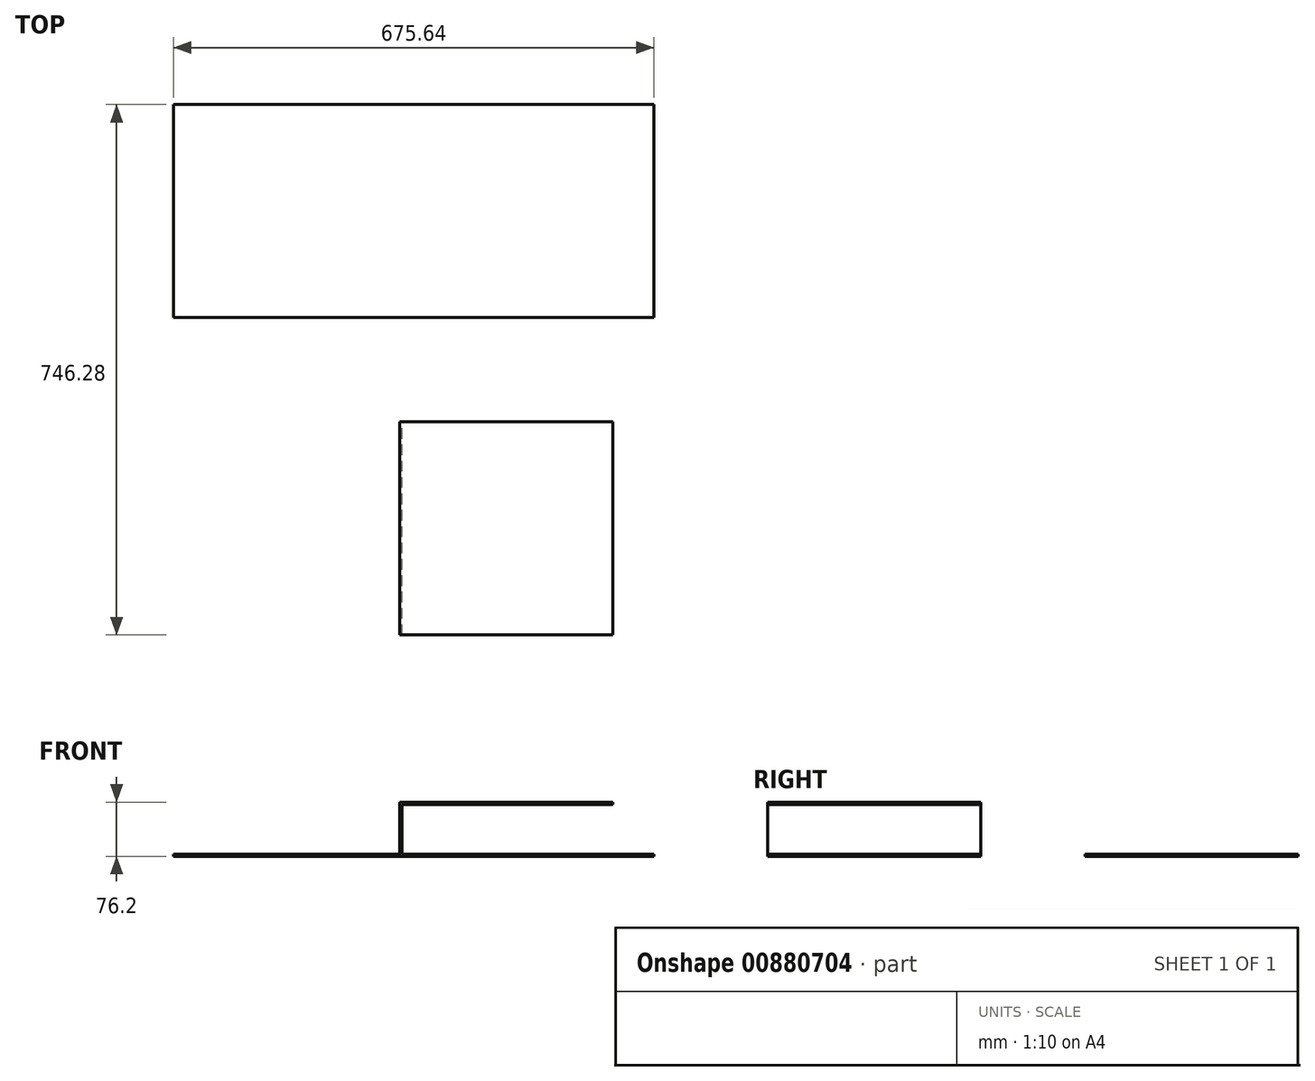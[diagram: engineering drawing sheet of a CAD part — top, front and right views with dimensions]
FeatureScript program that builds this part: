
annotation { "Feature Type Name" : "Feature", "Feature Type Description" : "" }
export const myFeature = defineFeature(function(context is Context, id is Id, definition is map)
    precondition{}
    {
        {
            var Q0;
            Q0=qCreatedBy(makeId("Front.planeOp"),FACE);
            var sketch = newSketch(context, id + "F0", { "sketchPlane" : qUnion([Q0])});
            skLineSegment(sketch, "E0", {"start": v(0, 0) * mm, "end": v(0, 76.2) * mm});
            skLineSegment(sketch, "E1", {"start": v(0, 76.2) * mm, "end": v(299.72, 76.2) * mm});
            skLineSegment(sketch, "E2", {"start": v(299.72, 76.2) * mm, "end": v(299.72, 73.03) * mm});
            skLineSegment(sketch, "E3", {"start": v(299.72, 73.03) * mm, "end": v(3.17, 73.02) * mm});
            skLineSegment(sketch, "E4", {"start": v(3.17, 73.02) * mm, "end": v(3.17, 3.17) * mm});
            skLineSegment(sketch, "E5", {"start": v(3.17, 3.17) * mm, "end": v(299.72, 3.18) * mm});
            skLineSegment(sketch, "E6", {"start": v(299.72, 3.18) * mm, "end": v(299.72, 0) * mm});
            skLineSegment(sketch, "E7", {"start": v(299.72, 0) * mm, "end": v(0, 0) * mm});
            skSolve(sketch);
        }
        {
            var Q0;
            Q0=makeQuery(id+"F0.imprint","IMPRINT",FACE,{"disambiguationData":[TD([[makeQuery(id+"F0.imprint","IMPRINT",EDGE,{"derivedFrom":sQuery(id+"F0.wireOp",EDGE,"E0")}),-1.0]])]});
            extrude(context, id + "F1", {"entities" : qUnion([Q0]), "depth" : 299.72 * mm, "offsetDistance" : 25.4 * mm});
        }
        {
            var Q0;
            Q0=qCreatedBy(makeId("Top.planeOp"),FACE);
            var sketch = newSketch(context, id + "F2", { "sketchPlane" : qUnion([Q0])});
            skLineSegment(sketch, "E8", {"start": v(-317.91, 146.84) * mm, "end": v(-18.2, 146.84) * mm});
            skLineSegment(sketch, "E9", {"start": v(-18.2, 146.84) * mm, "end": v(58, 146.84) * mm});
            skLineSegment(sketch, "E10", {"start": v(58, 146.84) * mm, "end": v(357.73, 146.84) * mm});
            skLineSegment(sketch, "E11", {"start": v(357.73, 146.84) * mm, "end": v(357.73, 446.56) * mm});
            skLineSegment(sketch, "E12", {"start": v(357.73, 446.56) * mm, "end": v(58, 446.56) * mm});
            skLineSegment(sketch, "E13", {"start": v(58, 446.56) * mm, "end": v(-18.2, 446.56) * mm});
            skLineSegment(sketch, "E14", {"start": v(-18.2, 446.56) * mm, "end": v(-317.91, 446.56) * mm});
            skLineSegment(sketch, "E15", {"start": v(-317.91, 446.56) * mm, "end": v(-317.91, 146.84) * mm});
            skSolve(sketch);
        }
        {
            var Q0;
            Q0=makeQuery(id+"F2.imprint","IMPRINT",FACE,{"disambiguationData":[TD([[makeQuery(id+"F2.imprint","IMPRINT",EDGE,{"derivedFrom":sQuery(id+"F2.wireOp",EDGE,"E8")}),1.0]])]});
            extrude(context, id + "F3", {"entities" : qUnion([Q0]), "depth" : 3.17 * mm, "offsetDistance" : 25.4 * mm});
        }
    });
